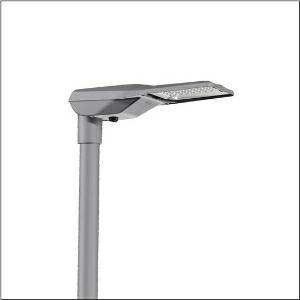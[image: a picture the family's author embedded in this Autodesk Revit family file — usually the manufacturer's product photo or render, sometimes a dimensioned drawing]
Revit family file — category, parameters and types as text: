
# Revit family: streetlight_sl_21_iq_mini___st1_0ab_5xe2m31u08gb_fb61
name_source: partatom
category: Lighting Fixtures
units: mm (PartAtom-declared; Revit-internal decimal feet)

## family parameters
Cut with Voids When Loaded = No
Host = Face
Light Source = No
Part Type = Normal
Room Calculation Point = No
Round Connector Dimension = Use Diameter
Shared = No

## types (1)
- --- (1 x LED, 5270 lm, 39.8 W, 3000K)
    Apparent Load = 40 VA
    CIE Flux Codes = 38 73 97 100 100
    Color Rendering = 70
    Color Temperature = 3000K
    Default Elevation = 1800 mm
    Description = Streetlight SL 21 iQ mini, mast luminaire, primary light control with lens, of PMMA, primary optical cover: cover, of toughened safety glass, transparent, light distribution: ST1.0aB, light emission: direct distribution, primary light characteristic: asymmetric, installation type: post-top, side-entry, LED, High Power LED, rated luminous flux: 5.270lm, luminous efficacy: 132lm/W, light colour: 730, colour temperature: 3000K, control gear: iQ-Street Remote, D4i with power reduction, control: pre-setting: logarithmic dimming characteristic, Street-Remote, Auto-Match, Temp-Guard, Lumen-Switch, Night-Set, Smart-Wire, Light-Fading, Desk-Remote (wireless, voltage-free reading and setting of iQ features in the workshop via application-optimized NFC function/RFID function), optimised constant luminous flux control (CLO 2.0), mains connection: 220..240V, AC, 50/60Hz, start of lifetime: 40W, end of service life: 41W, reduction: 18W, luminaire housing, of diecast aluminium, powder-coated, Siteco® metallic grey (DB 702S), corrosivity category C5 mid according to DIN EN ISO 12944, please order mast flange separately, inclination adjustable: 0°, 5°, 10°, 15°, sealing non-destructively replaceable, multi-level sealing system, length: 628mm, width: 235mm, height: 110mm, mast flange for spigot size: 42mm (side-entry): 5XC10008XM4, 60/48mm (side-entry/post-top): 5XC10108XM2, 76/60mm (side-entry/post-top): 5XC10108XM1, mounting height: 4..8m, Smart Interface below, protection rating (complete): IP66, insulation class (complete): insulation class II (safety insulation), certification: CE, ENEC, ENEC+, VDE, impact resistance: IK10, permissible operating ambient temperature for outdoor applications: -40..+50°C, standard-compliant lighting for roads and squares, packaging unit: 1 piece

Light Distribution: ST1.0aB
    Height = 110 mm
    Lamp = 1 x LED
    Lamp Light Flux = 5270 lm
    Lamp Power = 39.8 W
    Lamp count = 1
    Length = 625 mm
    Luminous efficacy = 132 lm/W
    Manufacturer = Siteco
    ModVariant = No
    Model = 5XE2M31U08GB
    Number of Poles = 1
    OnlyDefault = Yes
    Power Factor = 1
    Product Name = Streetlight SL 21 iQ mini | ST1.0aB
    Product group = mast luminaire | pylon top
    ProductGroupID = 6100
    Protection Class = Protection class II
    Protection Degree = IP 66
    RLX_Detail_Level = 1
    RLX_Emergency_Light_Flux = 0 lm
    RLX_Emergency_Type = 0
    RLX_Emergency_Type_DB = No
    RlxData = <blob elided: 92857 chars, md5=bf0dd0c8>
    Socket = socket
    Standby Power = 0 W
    System Light Flux = 5270 lm
    System Power = 40 W
    Type Comments = factory setting: luminous flux: 100 % | dim-lin: 254 | 800 mA
    Type Image = l_1003516.jpg
    URL = http://relux.com
    VarID = @adj_134071
    Voltage = 0 V
    Weight = 0.00 kg
    Width = 234 mm

## geometry (parser evidence)
native form markers: Blend x4, Sweep x10
no freeform markers — native parametric forms only
